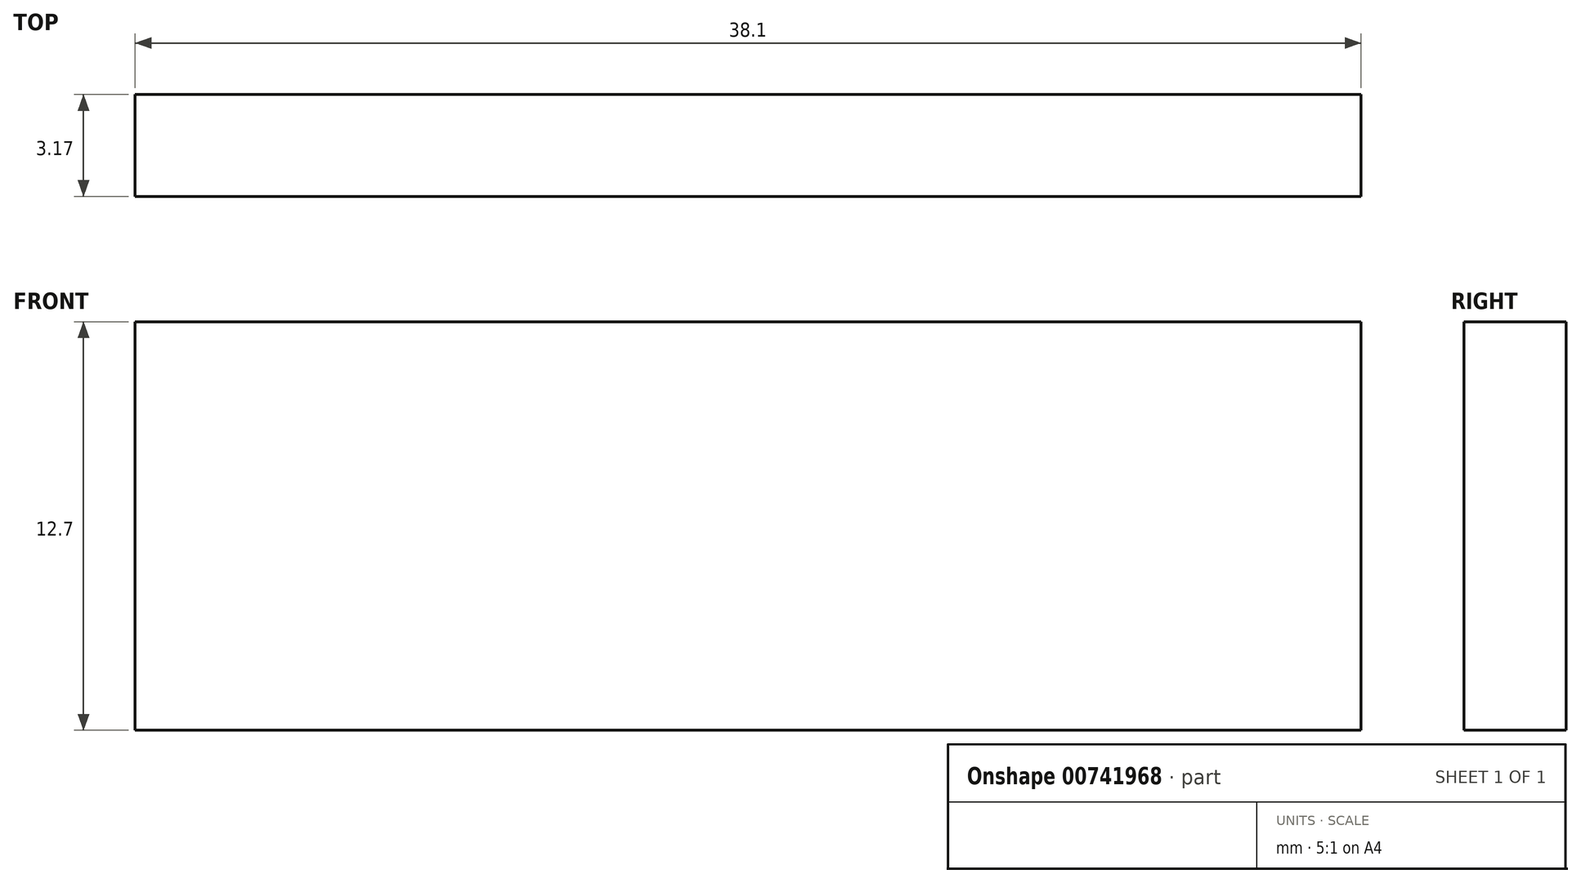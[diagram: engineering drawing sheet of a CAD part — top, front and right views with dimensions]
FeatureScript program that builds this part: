
annotation { "Feature Type Name" : "Feature", "Feature Type Description" : "" }
export const myFeature = defineFeature(function(context is Context, id is Id, definition is map)
    precondition{}
    {
        {
            var Q0;
            Q0=qCreatedBy(makeId("Front.planeOp"),FACE);
            var sketch = newSketch(context, id + "F0", { "sketchPlane" : qUnion([Q0])});
            skLineSegment(sketch, "E0.bottom", {"start": v(-29.11, -29.98) * mm, "end": v(8.99, -29.98) * mm});
            skLineSegment(sketch, "E0.top", {"start": v(-29.11, -42.68) * mm, "end": v(8.99, -42.68) * mm});
            skLineSegment(sketch, "E0.left", {"start": v(-29.11, -29.98) * mm, "end": v(-29.11, -42.68) * mm});
            skLineSegment(sketch, "E0.right", {"start": v(8.99, -29.98) * mm, "end": v(8.99, -42.68) * mm});
            skSolve(sketch);
        }
        {
            var Q0;
            Q0 = qSketchRegion(id + "F0", true);
            extrude(context, id + "F1", {"entities" : qUnion([Q0]), "depth" : 3.17 * mm, "offsetDistance" : 25.4 * mm});
        }
    });
